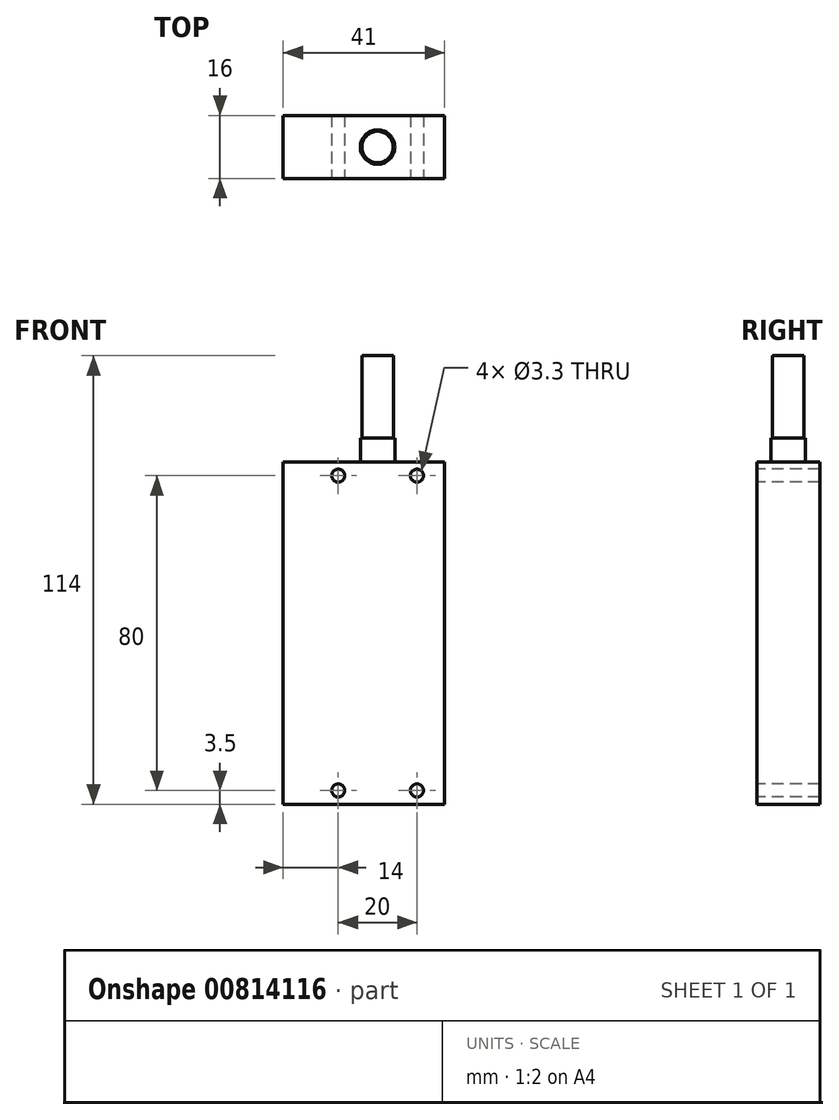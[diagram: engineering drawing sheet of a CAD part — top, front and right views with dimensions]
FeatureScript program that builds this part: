
annotation { "Feature Type Name" : "Feature", "Feature Type Description" : "" }
export const myFeature = defineFeature(function(context is Context, id is Id, definition is map)
    precondition{}
    {
        {
            var Q0;
            Q0=qCreatedBy(makeId("Front.planeOp"),FACE);
            var sketch = newSketch(context, id + "F0", { "sketchPlane" : qUnion([Q0])});
            skLineSegment(sketch, "E0.bottom", {"start": v(0, 0) * mm, "end": v(41, 0) * mm});
            skLineSegment(sketch, "E0.top", {"start": v(0, 87) * mm, "end": v(41, 87) * mm});
            skLineSegment(sketch, "E0.left", {"start": v(0, 0) * mm, "end": v(0, 87) * mm});
            skLineSegment(sketch, "E0.right", {"start": v(41, 0) * mm, "end": v(41, 87) * mm});
            skSolve(sketch);
        }
        {
            var Q0;
            Q0 = qSketchRegion(id + "F0", true);
            extrude(context, id + "F1", {"entities" : qUnion([Q0]), "depth" : 16 * mm, "offsetDistance" : 25 * mm});
        }
        {
            var Q0;
            Q0=makeQuery(id+"F1.opExtrude","CAP_FACE",FACE,{"disambiguationData":[OSD([sQuery(id+"F0.wireOp",EDGE,"E0.bottom"),sQuery(id+"F0.wireOp",EDGE,"E0.top"),sQuery(id+"F0.wireOp",EDGE,"E0.left"),sQuery(id+"F0.wireOp",EDGE,"E0.right")])],"isStart":false});
            var sketch = newSketch(context, id + "F2", { "sketchPlane" : qUnion([Q0])});
            skPoint(sketch, "E1", {"position": v(34, 83.5) * mm});
            skPoint(sketch, "E2", {"position": v(14, 83.5) * mm});
            skPoint(sketch, "E3", {"position": v(14, 3.5) * mm});
            skPoint(sketch, "E4", {"position": v(34, 3.5) * mm});
            skSolve(sketch);
        }
        {
            var Q0;
            Q0=sQuery(id+"F2.wireOp",VERTEX,"E2");
            var Q1;
            Q1=sQuery(id+"F2.wireOp",VERTEX,"E1");
            var Q2;
            Q2=sQuery(id+"F2.wireOp",VERTEX,"E3");
            var Q3;
            Q3=sQuery(id+"F2.wireOp",VERTEX,"E4");
            var Q4;
            Q4=makeQuery(id+"F1.opExtrude","SWEPT_BODY",BODY,{"disambiguationData":[OSD([sQuery(id+"F0.wireOp",EDGE,"E0.bottom"),sQuery(id+"F0.wireOp",EDGE,"E0.top"),sQuery(id+"F0.wireOp",EDGE,"E0.left"),sQuery(id+"F0.wireOp",EDGE,"E0.right")])]});
            hole(context, id + "F3", {"style" : HoleStyle.SIMPLE, "endStyle" : HoleEndStyle.BLIND, "standardTappedOrClearance" : lookupTablePath({ "standard" : "ISO", "engagement" : "75%", "pitch" : "0.7 mm", "size" : "M4", "type" : "Tapped" }), "standardBlindInLast" : lookupTablePath({ "standard" : "ISO", "engagement" : "75%", "pitch" : "0.7 mm", "size" : "M4", "type" : "Tapped" }), "holeDiameter" : 3.3 * mm, "majorDiameter" : 4 * mm, "showTappedDepth" : true, "holeDepth" : 27.7 * mm, "isTappedThrough" : true, "tappedDepth" : 25.6 * mm, "tapClearance" : 3, "locations" : qUnion([Q0, Q1, Q2, Q3]), "scope" : qUnion([Q4])});
        }
        {
            var Q0;
            Q0=makeQuery(id+"F1.opExtrude","SWEPT_FACE",FACE,{"disambiguationData":[OSD([sQuery(id+"F0.wireOp",EDGE,"E0.top")])]});
            var sketch = newSketch(context, id + "F4", { "sketchPlane" : qUnion([Q0])});
            skPoint(sketch, "E5.positionSnap0", {"position": v(41, -8) * mm});
            skPoint(sketch, "E6", {"position": v(24, -8) * mm});
            skCircle(sketch, "E7", {"center": v(24, -8) * mm, "radius": 4.38 * mm});
            skSolve(sketch);
        }
        {
            var Q0;
            Q0=makeQuery(id+"F4.imprint","IMPRINT",FACE,{"disambiguationData":[TD([[makeQuery(id+"F4.imprint","IMPRINT",EDGE,{"derivedFrom":sQuery(id+"F4.wireOp",EDGE,"E7")}),1.0]])]});
            extrude(context, id + "F5", {"entities" : qUnion([Q0]), "operationType" : NewBodyOperationType.ADD, "depth" : 6 * mm, "offsetDistance" : 25 * mm});
        }
        {
            var Q0;
            Q0=makeQuery(id+"F5.opExtrude","CAP_FACE",FACE,{"disambiguationData":[OSD([sQuery(id+"F4.wireOp",EDGE,"E7")])],"isStart":false});
            var sketch = newSketch(context, id + "F6", { "sketchPlane" : qUnion([Q0])});
            skCircle(sketch, "E8", {"center": v(24, -8) * mm, "radius": 4 * mm});
            skSolve(sketch);
        }
        {
            var Q0;
            Q0=makeQuery(id+"F6.imprint","IMPRINT",FACE,{"disambiguationData":[TD([[makeQuery(id+"F6.imprint","IMPRINT",EDGE,{"derivedFrom":sQuery(id+"F6.wireOp",EDGE,"E8")}),1.0]])]});
            extrude(context, id + "F7", {"entities" : qUnion([Q0]), "operationType" : NewBodyOperationType.ADD, "depth" : 21 * mm, "offsetDistance" : 25 * mm});
        }
    });
